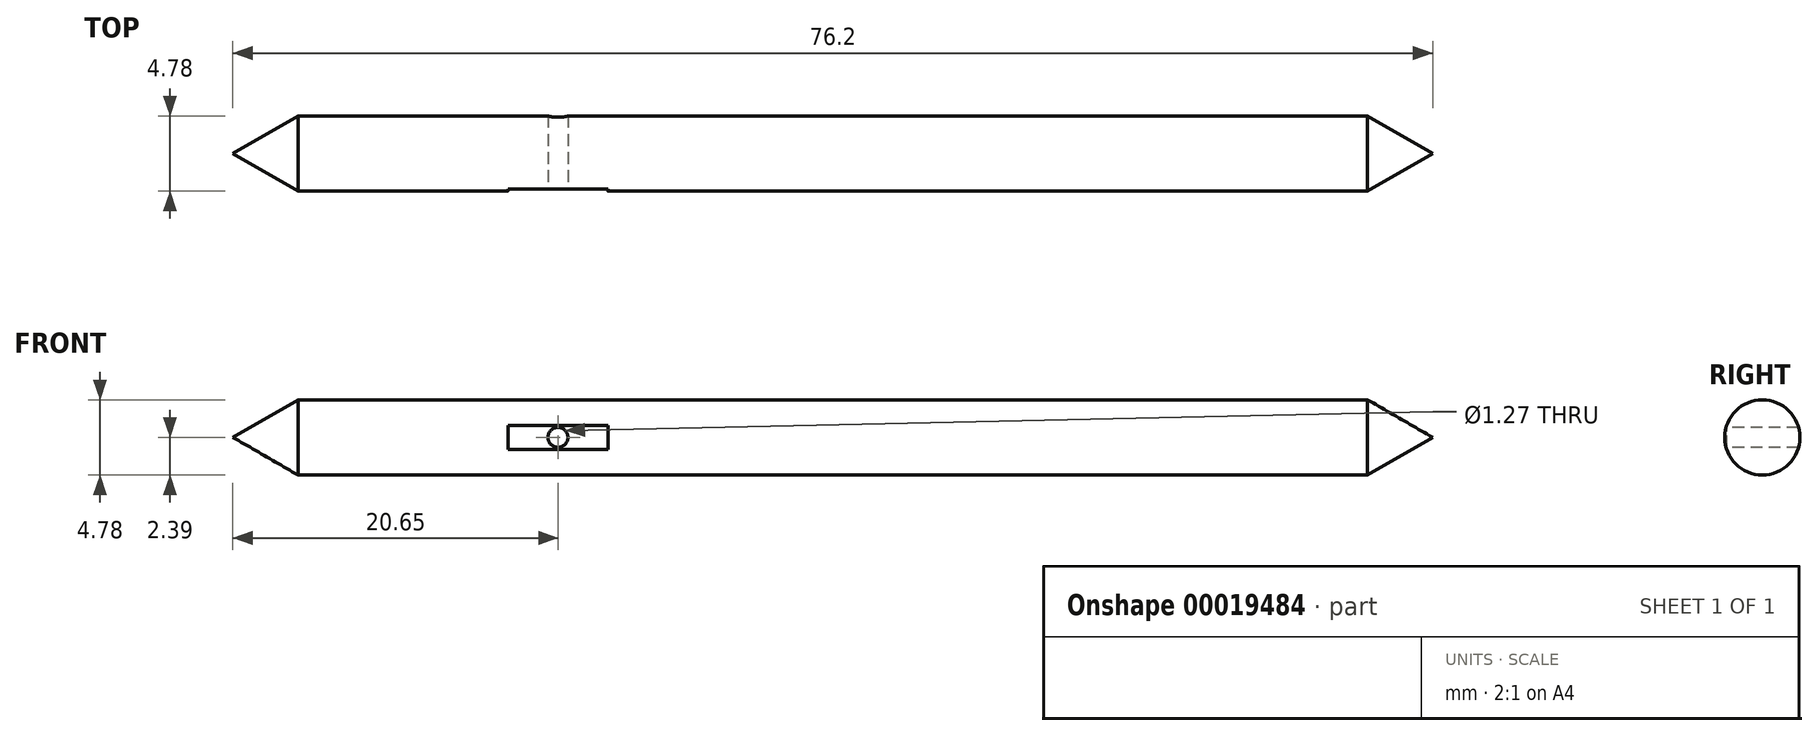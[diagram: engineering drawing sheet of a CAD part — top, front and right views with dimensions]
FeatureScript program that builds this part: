
annotation { "Feature Type Name" : "Feature", "Feature Type Description" : "" }
export const myFeature = defineFeature(function(context is Context, id is Id, definition is map)
    precondition{}
    {
        {
            var Q0;
            Q0=qCreatedBy(makeId("Front.planeOp"),FACE);
            var sketch = newSketch(context, id + "F0", { "sketchPlane" : qUnion([Q0])});
            skLineSegment(sketch, "E0", {"start": v(0, 0) * mm, "end": v(76.2, 0) * mm});
            skLineSegment(sketch, "E1", {"start": v(76.2, 0) * mm, "end": v(72.06, -2.39) * mm});
            skLineSegment(sketch, "E2", {"start": v(72.06, -2.39) * mm, "end": v(4.14, -2.39) * mm});
            skLineSegment(sketch, "E3", {"start": v(4.14, -2.39) * mm, "end": v(0, 0) * mm});
            skSolve(sketch);
        }
        {
            var Q0;
            Q0 = qSketchRegion(id + "F0", true);
            var Q1;
            Q1=sQuery(id+"F0.wireOp",EDGE,"E0");
            revolve(context, id + "F1", {"entities" : qUnion([Q0]), "axis" : qUnion([Q1]), "revolveType" : RevolveType.FULL});
        }
        {
            var Q0;
            Q0=qCreatedBy(makeId("Front.planeOp"),FACE);
            cPlane(context, id + "F2", {"entities" : qUnion([Q0]), "cplaneType" : CPlaneType.OFFSET, "offset" : 2.4 * mm, "width" : 152.4 * mm, "height" : 152.4 * mm});
        }
        {
            var Q0;
            Q0=qCreatedBy(id+"F2.planeOp",FACE);
            var sketch = newSketch(context, id + "F3", { "sketchPlane" : qUnion([Q0])});
            skLineSegment(sketch, "E4.rect.bottom", {"start": v(23.83, -1.27) * mm, "end": v(17.48, -1.27) * mm});
            skLineSegment(sketch, "E4.rect.top", {"start": v(23.83, 1.27) * mm, "end": v(17.48, 1.27) * mm});
            skLineSegment(sketch, "E4.rect.left", {"start": v(23.83, -1.27) * mm, "end": v(23.83, 1.27) * mm});
            skLineSegment(sketch, "E4.rect.right", {"start": v(17.48, -1.27) * mm, "end": v(17.48, 1.27) * mm});
            skPoint(sketch, "E5", {"position": v(20.65, 0) * mm});
            skCircle(sketch, "E6", {"center": v(20.65, 0) * mm, "radius": 0.64 * mm});
            skSolve(sketch);
        }
        {
            var Q0;
            Q0 = qSketchRegion(id + "F3", true);
            extrude(context, id + "F4", {"entities" : qUnion([Q0]), "operationType" : NewBodyOperationType.REMOVE, "oppositeDirection" : true, "depth" : 0.13 * mm});
        }
        {
            var Q0;
            Q0=makeQuery(id+"F3.imprint","IMPRINT",FACE,{"disambiguationData":[TD([[makeQuery(id+"F3.imprint","IMPRINT",EDGE,{"derivedFrom":sQuery(id+"F3.wireOp",EDGE,"E6")}),1.0]])]});
            extrude(context, id + "F5", {"entities" : qUnion([Q0]), "operationType" : NewBodyOperationType.REMOVE, "endBound" : BoundingType.THROUGH_ALL, "oppositeDirection" : true, "depth" : 25.4 * mm});
        }
    });
